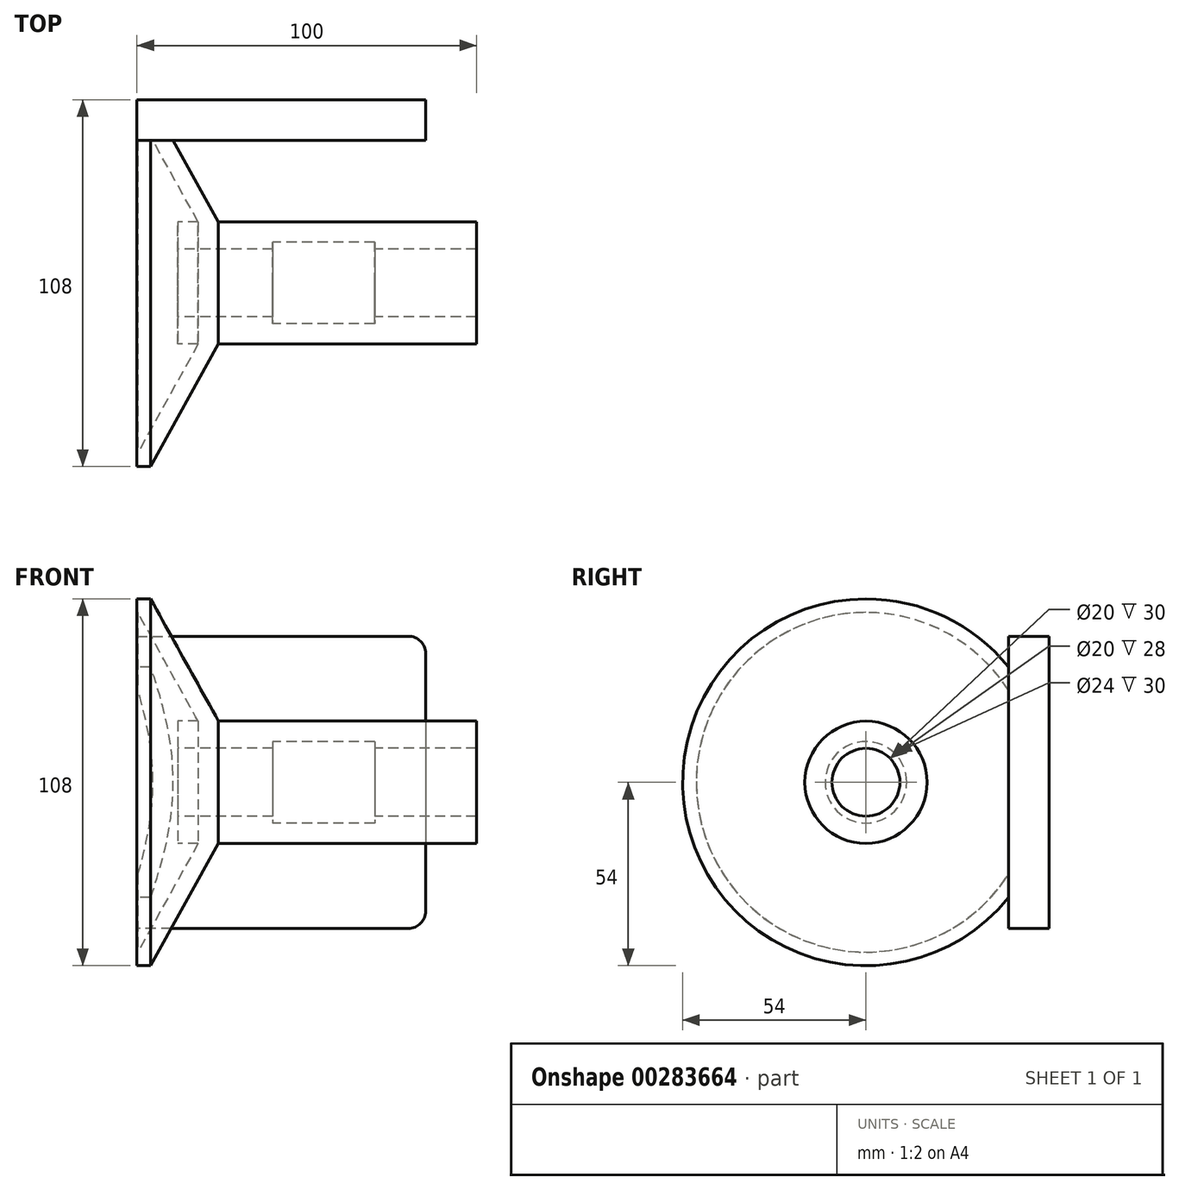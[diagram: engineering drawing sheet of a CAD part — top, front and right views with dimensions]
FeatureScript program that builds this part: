
annotation { "Feature Type Name" : "Feature", "Feature Type Description" : "" }
export const myFeature = defineFeature(function(context is Context, id is Id, definition is map)
    precondition{}
    {
        {
            var Q0;
            Q0=qCreatedBy(makeId("Top.planeOp"),FACE);
            var sketch = newSketch(context, id + "F0", { "sketchPlane" : qUnion([Q0])});
            skLineSegment(sketch, "E0", {"start": v(0, 0) * mm, "end": v(0, 18) * mm});
            skLineSegment(sketch, "E1", {"start": v(0, 18) * mm, "end": v(-76, 18) * mm});
            skLineSegment(sketch, "E2", {"start": v(-76, 18) * mm, "end": v(-96, 54) * mm});
            skLineSegment(sketch, "E3", {"start": v(-96, 54) * mm, "end": v(-100, 54) * mm});
            skLineSegment(sketch, "E4", {"start": v(-100, 54) * mm, "end": v(-100, 0) * mm});
            skLineSegment(sketch, "E5", {"start": v(-100, 0) * mm, "end": v(0, 0) * mm});
            skLineSegment(sketch, "E6", {"start": v(0, 10) * mm, "end": v(-30, 10) * mm});
            skLineSegment(sketch, "E7", {"start": v(-30, 10) * mm, "end": v(-30, 12) * mm});
            skLineSegment(sketch, "E8", {"start": v(-60, 12) * mm, "end": v(-60, 10) * mm});
            skLineSegment(sketch, "E9", {"start": v(-60, 10) * mm, "end": v(-88, 10) * mm});
            skLineSegment(sketch, "E10", {"start": v(-88, 10) * mm, "end": v(-88, 18) * mm});
            skLineSegment(sketch, "E11", {"start": v(-88, 18) * mm, "end": v(-82, 18) * mm});
            skLineSegment(sketch, "E12.0", {"start": v(-82, 18) * mm, "end": v(-99.78, 50) * mm});
            skLineSegment(sketch, "E13.0", {"start": v(-99.78, 50) * mm, "end": v(-100, 50) * mm});
            skLineSegment(sketch, "E14", {"start": v(-30, 12) * mm, "end": v(-60, 12) * mm});
            skSolve(sketch);
        }
        {
            var Q0;
            {var subQ4=sQuery(id+"F0.wireOp",EDGE,"E1");Q0=makeQuery(id+"F0.imprint","IMPRINT",FACE,{"disambiguationData":[TD([[makeQuery(id+"F0.imprint","IMPRINT",EDGE,{"derivedFrom":subQ4}),1.0]])]});}
            var Q1;
            Q1=sQuery(id+"F0.wireOp",EDGE,"E5");
            revolve(context, id + "F1", {"entities" : qUnion([Q0]), "axis" : qUnion([Q1]), "revolveType" : RevolveType.FULL});
        }
        {
            var Q0;
            Q0=qCreatedBy(makeId("Front.planeOp"),FACE);
            cPlane(context, id + "F2", {"entities" : qUnion([Q0]), "cplaneType" : CPlaneType.OFFSET, "offset" : 54 * mm, "oppositeDirection" : true, "width" : 150 * mm, "height" : 150 * mm});
        }
        {
            var Q0;
            Q0=qCreatedBy(id+"F2.planeOp",FACE);
            var sketch = newSketch(context, id + "F3", { "sketchPlane" : qUnion([Q0])});
            skLineSegment(sketch, "E15.0", {"start": v(-100, -54) * mm, "end": v(-100, 54) * mm});
            skLineSegment(sketch, "E16", {"start": v(-100, 43) * mm, "end": v(-20, 43) * mm});
            skLineSegment(sketch, "E17", {"start": v(-15, 38) * mm, "end": v(-15, -38) * mm});
            skLineSegment(sketch, "E18", {"start": v(-20, -43) * mm, "end": v(-100, -43) * mm});
            skLineSegment(sketch, "E19", {"start": v(0, 0) * mm, "end": v(-137.96, 0) * mm, "construction": true});
            skPoint(sketch, "E20.visualSharp", {"position": v(-15, 43) * mm});
            skArc(sketch, "E20.filletArc", {"start": v(-15, 38) * mm, "mid": v(-16.46, 41.54) * mm, "end": v(-20, 43) * mm});
            skPoint(sketch, "E21.visualSharp", {"position": v(-15, -43) * mm});
            skArc(sketch, "E21.filletArc", {"start": v(-20, -43) * mm, "mid": v(-16.46, -41.54) * mm, "end": v(-15, -38) * mm});
            skSolve(sketch);
        }
        {
            var Q0;
            Q0 = qSketchRegion(id + "F3", true);
            extrude(context, id + "F4", {"entities" : qUnion([Q0]), "operationType" : NewBodyOperationType.ADD, "depth" : 12 * mm});
        }
    });
